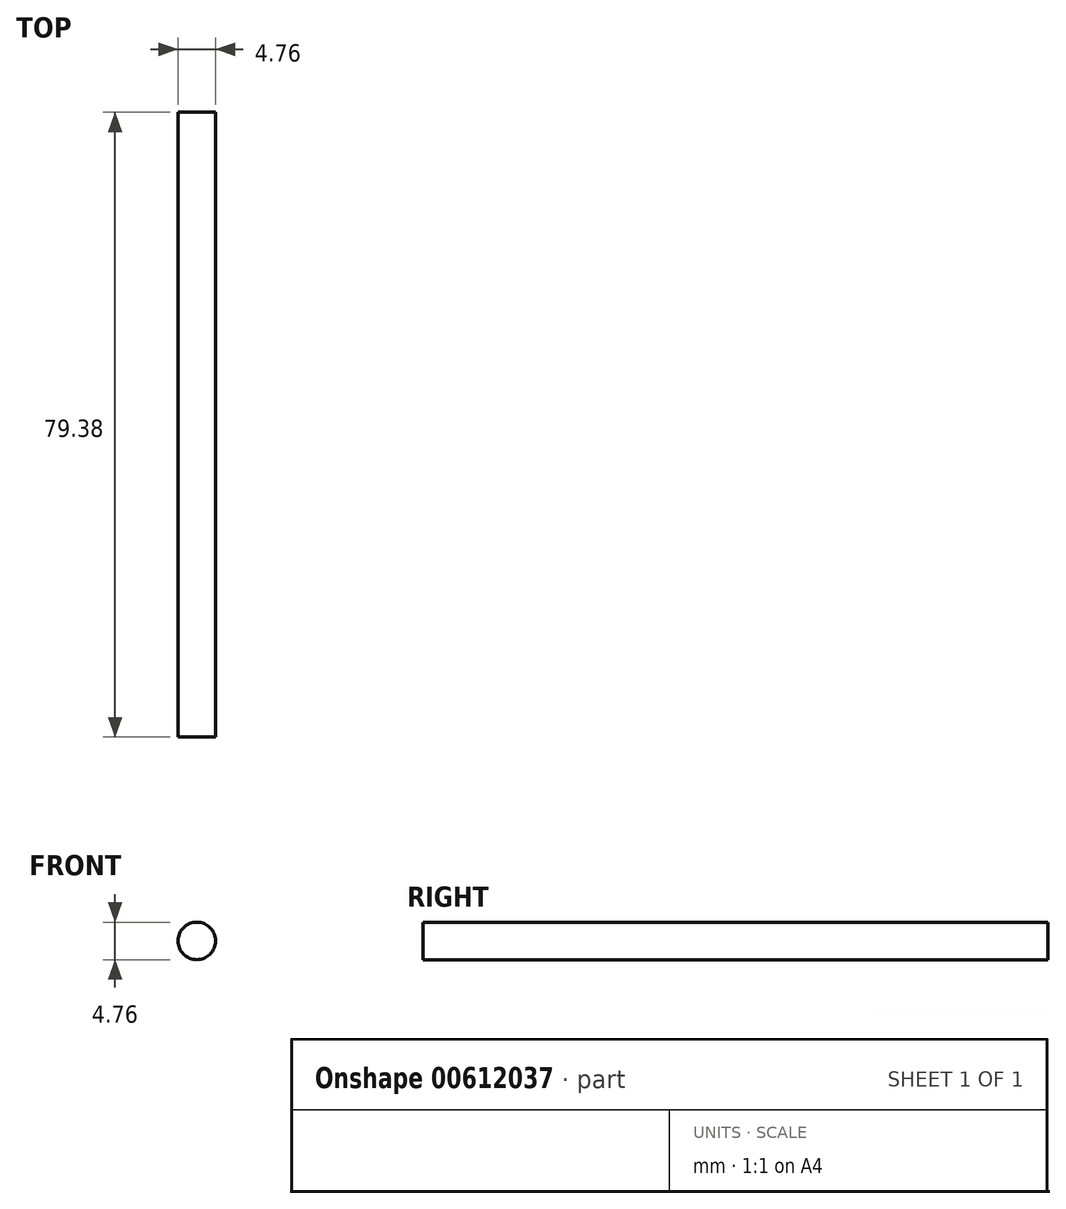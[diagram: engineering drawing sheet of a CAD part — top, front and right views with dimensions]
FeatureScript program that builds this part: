
annotation { "Feature Type Name" : "Feature", "Feature Type Description" : "" }
export const myFeature = defineFeature(function(context is Context, id is Id, definition is map)
    precondition{}
    {
        {
            var Q0;
            Q0=qCreatedBy(makeId("Front.planeOp"),FACE);
            var sketch = newSketch(context, id + "F0", { "sketchPlane" : qUnion([Q0])});
            skCircle(sketch, "E0", {"center": v(0, 0) * mm, "radius": 2.38 * mm});
            skSolve(sketch);
        }
        {
            var Q0;
            Q0 = qSketchRegion(id + "F0", true);
            extrude(context, id + "F1", {"entities" : qUnion([Q0]), "depth" : 79.38 * mm, "offsetDistance" : 25.4 * mm});
        }
    });
